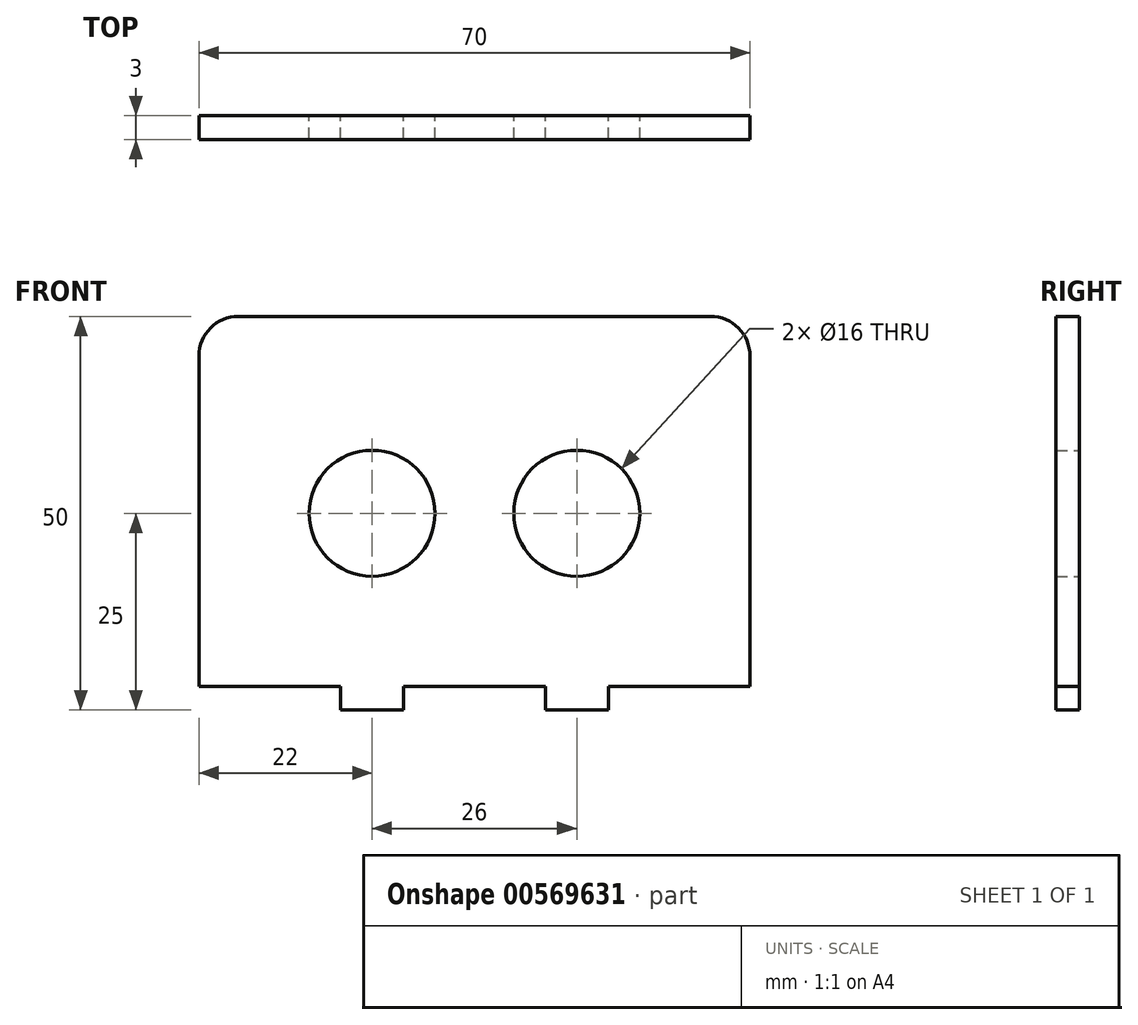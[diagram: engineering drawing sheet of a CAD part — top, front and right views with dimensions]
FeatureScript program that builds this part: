
annotation { "Feature Type Name" : "Feature", "Feature Type Description" : "" }
export const myFeature = defineFeature(function(context is Context, id is Id, definition is map)
    precondition{}
    {
        {
            var Q0;
            Q0=qCreatedBy(makeId("Front.planeOp"),FACE);
            var sketch = newSketch(context, id + "F0", { "sketchPlane" : qUnion([Q0])});
            skLineSegment(sketch, "E0.bottom", {"start": v(-30, 25) * mm, "end": v(30, 25) * mm});
            skLineSegment(sketch, "E0.top", {"start": v(-17, -25) * mm, "end": v(-9, -25) * mm});
            skLineSegment(sketch, "E0.left", {"start": v(-35, 20) * mm, "end": v(-35, -25) * mm});
            skLineSegment(sketch, "E0.right", {"start": v(35, 20) * mm, "end": v(35, -25) * mm});
            skLineSegment(sketch, "E1", {"start": v(-55.61, 0) * mm, "end": v(43.67, 0) * mm, "construction": true});
            skCircle(sketch, "E2", {"center": v(-13, 0) * mm, "radius": 8 * mm});
            skCircle(sketch, "E3", {"center": v(13, 0) * mm, "radius": 8 * mm});
            skPoint(sketch, "E4.visualSharp", {"position": v(-35, 25) * mm});
            skArc(sketch, "E4.filletArc", {"start": v(-30, 25) * mm, "mid": v(-33.54, 23.54) * mm, "end": v(-35, 20) * mm});
            skPoint(sketch, "E5.visualSharp", {"position": v(35, 25) * mm});
            skArc(sketch, "E5.filletArc", {"start": v(35, 20) * mm, "mid": v(33.54, 23.54) * mm, "end": v(30, 25) * mm});
            skLineSegment(sketch, "E6", {"start": v(-35, -22) * mm, "end": v(44.14, -22) * mm, "construction": true});
            skLineSegment(sketch, "E7", {"start": v(-17, -25) * mm, "end": v(-17, -22) * mm});
            skLineSegment(sketch, "E8", {"start": v(-17, -22) * mm, "end": v(-17, -25) * mm});
            skLineSegment(sketch, "E9", {"start": v(-9, -25) * mm, "end": v(-9, -22) * mm});
            skLineSegment(sketch, "E10", {"start": v(-9, -22) * mm, "end": v(9, -22) * mm});
            skLineSegment(sketch, "E11", {"start": v(9, -22) * mm, "end": v(9, -25) * mm});
            skLineSegment(sketch, "E12", {"start": v(9, -25) * mm, "end": v(17, -25) * mm});
            skLineSegment(sketch, "E13", {"start": v(17, -25) * mm, "end": v(17, -22) * mm});
            skLineSegment(sketch, "E14", {"start": v(17, -22) * mm, "end": v(35, -22) * mm});
            skLineSegment(sketch, "E15", {"start": v(-35, -22) * mm, "end": v(-17, -22) * mm});
            skSolve(sketch);
        }
        {
            var Q0;
            Q0=makeQuery(id+"F0.imprint","IMPRINT",FACE,{"disambiguationData":[TD([[makeQuery(id+"F0.imprint","IMPRINT",EDGE,{"derivedFrom":sQuery(id+"F0.wireOp",EDGE,"E0.bottom")}),-1.0]])]});
            extrude(context, id + "F1", {"entities" : qUnion([Q0]), "depth" : 3 * mm, "offsetDistance" : 25 * mm});
        }
    });
